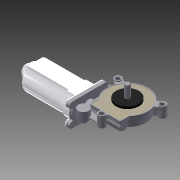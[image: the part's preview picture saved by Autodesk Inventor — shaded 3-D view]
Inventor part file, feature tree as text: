
AUTODESK INVENTOR PART (.ipt)
format: ipt  version: 2011 (Build 150239000, 239)  size: 618,496 bytes
history: native  units: mm
features: sketch x28, extrude x24, fillet x7, projected_geometry x5, rib x4, other x3, chamfer x2, plane x2, pattern_circular x1, hole x1
ambient origin geometry x8: Origin, YZ Plane, XZ Plane, XY Plane, X Axis, Y Axis, Z Axis, Center Point
bodies: Solid1 (feature_tree)
feature tree (77):
  extrude  "Extrusion1"  Depth=50.0mm
  extrude  "Extrusion2"  Depth=5.6mm TaperAngle=0.0deg
  extrude  "Extrusion3"  Depth=12.3mm TaperAngle=0.0deg
  extrude  "Extrusion4"  Depth=1.5mm TaperAngle=0.0deg
  extrude  "Extrusion5"  Depth=2.0mm TaperAngle=0.0deg
  extrude  "Extrusion6"  Depth=10.0mm
  rib  "Rib1"
  fillet  "Fillet1"  Radius=1.0mm
  pattern_circular  "Circular Pattern1"  Count=8 Angle=360.0deg
  extrude  "Extrusion9"  Depth=11.5mm
  extrude  "Extrusion7"  Depth=36.27mm
  extrude  "Extrusion8"  Depth=20.98mm
  rib  "Rib2"
  extrude  "Extrusion10"  Depth=10.5mm TaperAngle=0.0deg
  hole  "Hole2"  [1 undecoded]
  chamfer  "Chamfer1"  Distance=0.5mm
  extrude  "Extrusion11"  Depth=0.7mm TaperAngle=45.0deg
  extrude  "Extrusion12"  Depth=3.5mm TaperAngle=0.0deg
  chamfer  "Chamfer2"  Distance=20.0mm
  extrude  "Extrusion13"  Depth=0.7mm TaperAngle=45.0deg
  plane  "Work Plane1"
  extrude  "Extrusion14"  Depth=14.0mm
  fillet  "Fillet2"  Radius=30.0mm
  sketch  "Sketch20"  dims[d62=37.25mm d63=3.5mm d64=0.0mm d65=20.0mm d66=0.0mm]
  extrude  "Extrusion15"  [1 undecoded]
  extrude  "Extrusion17"  Depth=9.9mm
  extrude  "Extrusion18"  Depth=5.0mm TaperAngle=0.0deg
  extrude  "Extrusion19"  Depth=5.0mm
  extrude  "Extrusion20"  Depth=64.0mm
  extrude  "Extrusion21"  Depth=2.0mm TaperAngle=0.0deg
  fillet  "Fillet3"  Radius=48.8mm
  extrude  "Extrusion22"  Depth=45.5mm
  other  "Work Axis1"
  plane  "Work Plane3"
  rib  "Rib3"
  sketch  "Sketch30"  dims[d88=0.5mm d89=0.0mm d92=2.0mm d93=0.0mm d94=48.8mm]
  extrude  "Extrusion23"  Depth=28.6mm
  extrude  "Extrusion24"  Depth=8.0mm TaperAngle=0.0deg
  extrude  "Extrusion26"  Depth=20.0mm
  rib  "Rib4"
  fillet  "Fillet4"  Radius=7.4mm
  fillet  "Fillet5"  Radius=1.5mm
  fillet  "Fillet6"  Radius=18.0mm
  fillet  "Fillet7"  Radius=10.0mm
  other  "Emboss_LH"
  sketch  "Sketch1"  dims[d0=67.0mm d1=50.0mm]
  sketch  "Sketch2"  dims[d2=37.0mm d3=5.6mm d4=0.0mm]
  sketch  "Sketch3"  dims[d5=3.0mm d6=12.3mm d7=0.0mm]
  sketch  "Sketch4"  dims[d8=42.0mm d9=1.5mm d10=0.0mm]
  sketch  "Sketch5"  dims[d11=21.0mm d12=2.0mm d13=0.0mm]
  sketch  "Sketch6"  dims[d14=8.75mm d15=0.0mm d16=10.0mm d17=1.0mm d18=0.0mm]
  sketch  "Sketch7"  dims[d19=1.5mm]
  other  "embossLH"
  sketch  "Sketch9"  dims[d20=1.0mm]
  sketch  "Sketch10"  dims[d21=1.5mm d22=0.0mm d23=80.0mm d24=360.0deg]
  sketch  "Sketch11"  dims[d26=0.3mm d27=0.0mm d28=11.5mm]
  projected_geometry  "Projected Loop1"
  projected_geometry  "Projected Loop2"
  projected_geometry  "Projected Loop3"
  sketch  "Sketch13"  dims[d29=36.27mm d30=36.27mm]
  sketch  "Sketch14"  dims[d31=41.84mm d32=20.98mm]
  sketch  "Sketch15"  dims[d33=1.0mm d34=0.0mm d35=10.5mm d36=0.0mm]
  projected_geometry  "Projected Loop4"
  projected_geometry  "Projected Loop5"
  sketch  "Sketch16"  dims[d37=3.0mm d38=1.0mm d39=0.0mm]
  sketch  "Sketch17"  dims[d47=1.2mm d48=0.5mm d49=0.0mm]
  sketch  "Sketch18"  dims[d50=1.5mm d51=0.0mm]
  sketch  "Sketch19"  dims[d52=7.1mm d53=6.0mm d54=4.0mm d55=2.0mm d56=90.0deg d57=7.1mm d58=20.594885mm d59=0.7mm d60=2.0mm d61=45.0deg]
  sketch  "Sketch23"  dims[d67=7.95mm d68=0.7mm d69=2.0mm d70=45.0deg]
  sketch  "Sketch24"  dims[d71=10.0mm d72=14.0mm d73=30.0mm]
  sketch  "Sketch25"  dims[d74=20.0mm d75=0.0mm d76=-38.0mm]
  sketch  "Sketch26"  dims[d77=37.9mm d79=9.9mm]
  sketch  "Sketch27"  dims[d80=25.0mm d81=5.0mm d82=0.0mm]
  sketch  "Sketch28"  dims[d84=1.5mm d85=5.0mm]
  sketch  "Sketch29"  dims[d86=18.0mm d87=64.0mm]
  sketch  "Sketch31"  dims[d95=13.0mm d96=0.0mm d97=45.5mm]
  sketch  "Sketch33"  dims[d98=67.0mm d99=0.0mm d100=28.6mm d101=8.0mm d102=0.0mm d103=20.0mm d104=7.4mm d105=-2.617994mm d106=1.5mm d107=18.0mm d108=10.0mm d109=0.0mm d110=1.5mm d111=1.0mm d112=0.0mm d113=17.5mm d114=10.6mm d115=0.0mm d116=3.0mm d117=0.0mm d118=10.7mm d121=6.9mm d122=4.6mm d123=0.0mm d124=2.0mm d125=1.0mm d126=0.0mm d127=1.5mm d128=0.5mm d129=1.0mm d130=2.0mm d131=0.2mm d132=48.8mm d134=45.5mm]
note: 2 required parameter values undecoded (feature->parameter linkage not recoverable at this tier; creation-order binding heuristic only, values carry confidence <= 0.55)
